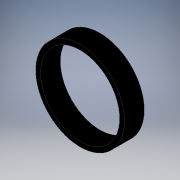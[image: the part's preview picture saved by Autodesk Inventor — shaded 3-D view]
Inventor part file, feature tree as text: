
AUTODESK INVENTOR PART (.ipt)
format: ipt  version: 2018 (Build 220112000, 112)  size: 98,304 bytes
history: native  units: in
note: dims shown in document units (in); Inventor stores cm internally (conversion verified against a paired STEP export)
features: extrude x1, sketch x1
ambient origin geometry x8: Origin, YZ Plane, XZ Plane, XY Plane, X Axis, Y Axis, Z Axis, Center Point
bodies: Solid1 (feature_tree)
feature tree (2):
  extrude  "Extrusion1"  Depth=1.0in
  sketch  "Sketch1"  dims[d0=4.0in d1=4.5in d2=1.0in d3=0.0in]
